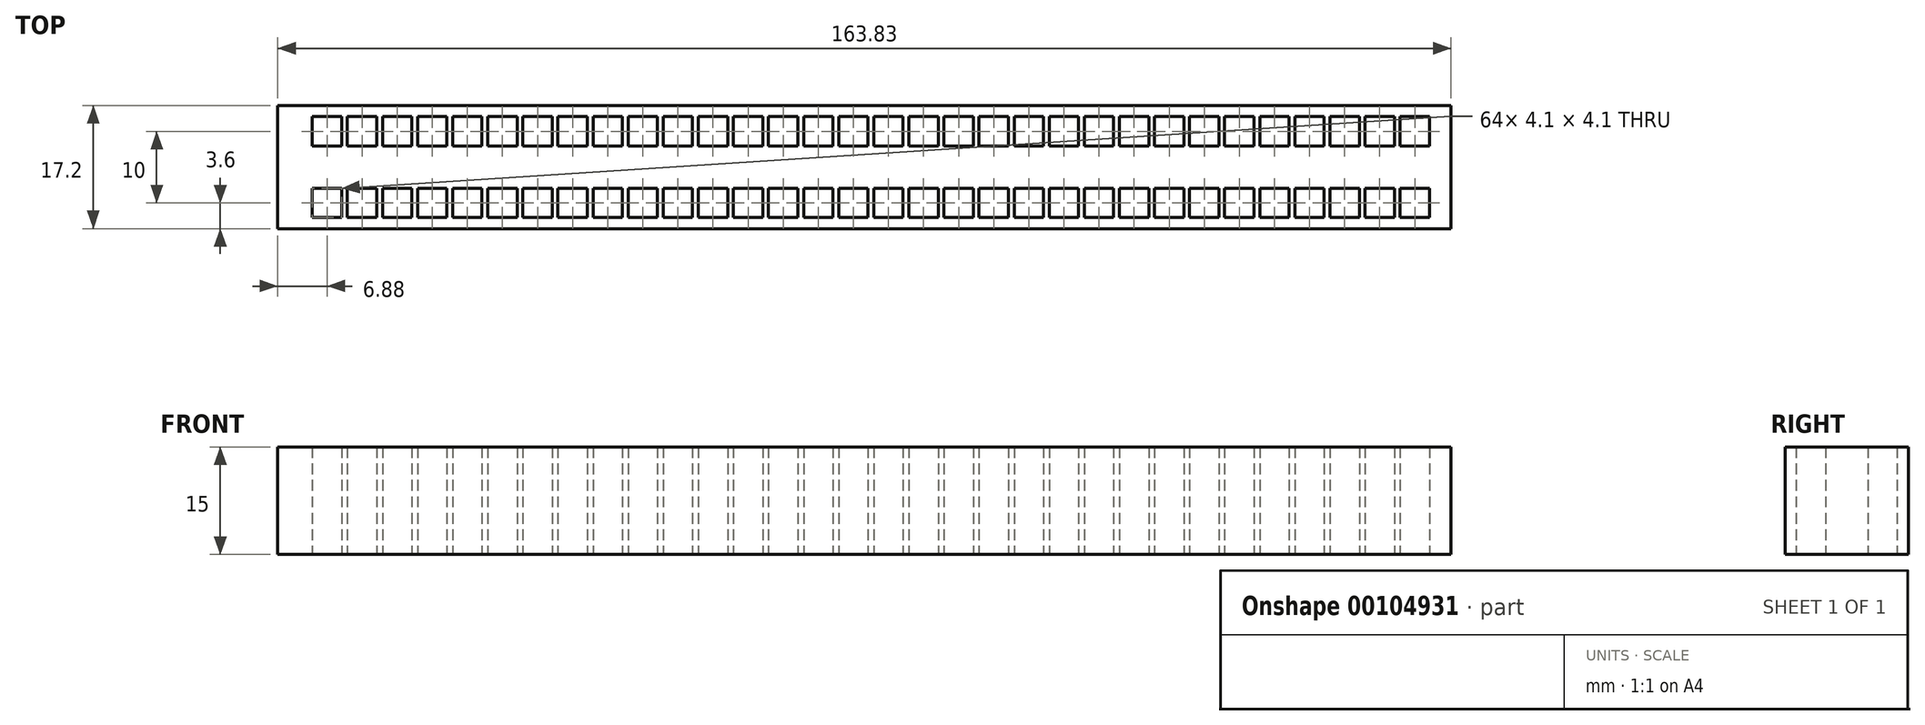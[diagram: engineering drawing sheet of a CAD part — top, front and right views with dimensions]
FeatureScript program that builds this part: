
annotation { "Feature Type Name" : "Feature", "Feature Type Description" : "" }
export const myFeature = defineFeature(function(context is Context, id is Id, definition is map)
    precondition{}
    {
        {
            var Q0;
            Q0=qCreatedBy(makeId("Top.planeOp"),FACE);
            var sketch = newSketch(context, id + "F0", { "sketchPlane" : qUnion([Q0])});
            skLineSegment(sketch, "E0", {"start": v(0, 0) * mm, "end": v(-105.59, 0) * mm});
            skLineSegment(sketch, "E1", {"start": v(0, 5) * mm, "end": v(-102.01, 5) * mm});
            skLineSegment(sketch, "E2", {"start": v(0, -8) * mm, "end": v(-106.05, -8) * mm});
            skLineSegment(sketch, "E3.bottom", {"start": v(-4.5, 7.05) * mm, "end": v(-0.4, 7.05) * mm});
            skLineSegment(sketch, "E3.top", {"start": v(-4.5, 2.95) * mm, "end": v(-0.4, 2.95) * mm});
            skLineSegment(sketch, "E3.left", {"start": v(-4.5, 7.05) * mm, "end": v(-4.5, 2.95) * mm});
            skLineSegment(sketch, "E3.right", {"start": v(-0.4, 7.05) * mm, "end": v(-0.4, 2.95) * mm});
            skPoint(sketch, "E3.middle", {"position": v(-2.45, 5) * mm});
            skLineSegment(sketch, "E4", {"start": v(0, 0) * mm, "end": v(0, 8.6) * mm, "construction": true});
            skLineSegment(sketch, "E5", {"start": v(-4.9, 0) * mm, "end": v(-4.9, 10.23) * mm, "construction": true});
            skLineSegment(sketch, "E6.MirrorCS", {"start": v(-5.3, 2.95) * mm, "end": v(-9.4, 2.95) * mm});
            skLineSegment(sketch, "E7.MirrorCS", {"start": v(-5.3, 7.05) * mm, "end": v(-5.3, 2.95) * mm});
            skLineSegment(sketch, "E8.MirrorCS", {"start": v(-5.3, 7.05) * mm, "end": v(-9.4, 7.05) * mm});
            skPoint(sketch, "E9.MirrorP", {"position": v(-7.35, 5) * mm});
            skLineSegment(sketch, "E10.MirrorCS", {"start": v(-9.4, 7.05) * mm, "end": v(-9.4, 2.95) * mm});
            skLineSegment(sketch, "E11.MirrorCS", {"start": v(-9.8, 0) * mm, "end": v(-9.8, 8.6) * mm, "construction": true});
            skLineSegment(sketch, "E12.MirrorCS", {"start": v(-9.8, 5) * mm, "end": v(92.21, 5) * mm});
            skLineSegment(sketch, "E13.MirrorCS", {"start": v(-19.6, 5) * mm, "end": v(82.41, 5) * mm, "construction": true});
            skLineSegment(sketch, "E14.MirrorCS", {"start": v(-15.1, 7.05) * mm, "end": v(-15.1, 2.95) * mm});
            skLineSegment(sketch, "E15.MirrorCS", {"start": v(-14.7, 0) * mm, "end": v(-14.7, 10.23) * mm, "construction": true});
            skLineSegment(sketch, "E16.MirrorCS", {"start": v(-19.2, 7.05) * mm, "end": v(-19.2, 2.95) * mm});
            skLineSegment(sketch, "E17.MirrorCS", {"start": v(-15.1, 2.95) * mm, "end": v(-19.2, 2.95) * mm});
            skLineSegment(sketch, "E18.MirrorCS", {"start": v(-15.1, 7.05) * mm, "end": v(-19.2, 7.05) * mm});
            skPoint(sketch, "E19.MirrorP", {"position": v(-17.15, 5) * mm});
            skPoint(sketch, "E20.MirrorP", {"position": v(-12.25, 5) * mm});
            skLineSegment(sketch, "E21.MirrorCS", {"start": v(-19.6, 0) * mm, "end": v(-19.6, 8.6) * mm, "construction": true});
            skLineSegment(sketch, "E22.MirrorCS", {"start": v(-14.3, 2.95) * mm, "end": v(-10.2, 2.95) * mm});
            skLineSegment(sketch, "E23.MirrorCS", {"start": v(-14.3, 7.05) * mm, "end": v(-14.3, 2.95) * mm});
            skLineSegment(sketch, "E24.MirrorCS", {"start": v(-14.3, 7.05) * mm, "end": v(-10.2, 7.05) * mm});
            skLineSegment(sketch, "E25.MirrorCS", {"start": v(-10.2, 7.05) * mm, "end": v(-10.2, 2.95) * mm});
            skLineSegment(sketch, "E26.MirrorCS", {"start": v(-9.8, 5) * mm, "end": v(-111.81, 5) * mm});
            skLineSegment(sketch, "E27.MirrorCS", {"start": v(-29.4, 5) * mm, "end": v(-131.41, 5) * mm});
            skLineSegment(sketch, "E28.MirrorCS", {"start": v(-29.4, 5) * mm, "end": v(72.61, 5) * mm});
            skLineSegment(sketch, "E29.MirrorCS", {"start": v(-24.5, 0) * mm, "end": v(-24.5, 10.23) * mm, "construction": true});
            skLineSegment(sketch, "E30.MirrorCS", {"start": v(-29.4, 0) * mm, "end": v(-29.4, 8.6) * mm, "construction": true});
            skLineSegment(sketch, "E31.MirrorCS", {"start": v(-24.9, 7.05) * mm, "end": v(-29, 7.05) * mm});
            skLineSegment(sketch, "E32.MirrorCS", {"start": v(-34.7, 7.05) * mm, "end": v(-38.8, 7.05) * mm});
            skLineSegment(sketch, "E33.MirrorCS", {"start": v(-19.6, 5) * mm, "end": v(-121.61, 5) * mm});
            skPoint(sketch, "E34.MirrorP", {"position": v(-22.05, 5) * mm});
            skPoint(sketch, "E35.MirrorP", {"position": v(-36.75, 5) * mm});
            skLineSegment(sketch, "E36.MirrorCS", {"start": v(-39.2, 5) * mm, "end": v(62.81, 5) * mm});
            skLineSegment(sketch, "E37.MirrorCS", {"start": v(-24.1, 2.95) * mm, "end": v(-20, 2.95) * mm});
            skLineSegment(sketch, "E38.MirrorCS", {"start": v(-34.7, 2.95) * mm, "end": v(-38.8, 2.95) * mm});
            skLineSegment(sketch, "E39.MirrorCS", {"start": v(-34.7, 7.05) * mm, "end": v(-34.7, 2.95) * mm});
            skLineSegment(sketch, "E40.MirrorCS", {"start": v(-38.8, 7.05) * mm, "end": v(-38.8, 2.95) * mm});
            skLineSegment(sketch, "E41.MirrorCS", {"start": v(-39.2, 0) * mm, "end": v(-39.2, 8.6) * mm, "construction": true});
            skLineSegment(sketch, "E42.MirrorCS", {"start": v(-34.3, 0) * mm, "end": v(-34.3, 10.23) * mm, "construction": true});
            skLineSegment(sketch, "E43.MirrorCS", {"start": v(-33.9, 2.95) * mm, "end": v(-29.8, 2.95) * mm});
            skLineSegment(sketch, "E44.MirrorCS", {"start": v(-33.9, 7.05) * mm, "end": v(-33.9, 2.95) * mm});
            skLineSegment(sketch, "E45.MirrorCS", {"start": v(-33.9, 7.05) * mm, "end": v(-29.8, 7.05) * mm});
            skLineSegment(sketch, "E46.MirrorCS", {"start": v(-29.8, 7.05) * mm, "end": v(-29.8, 2.95) * mm});
            skLineSegment(sketch, "E47.MirrorCS", {"start": v(-29, 7.05) * mm, "end": v(-29, 2.95) * mm});
            skLineSegment(sketch, "E48.MirrorCS", {"start": v(-24.9, 7.05) * mm, "end": v(-24.9, 2.95) * mm});
            skLineSegment(sketch, "E49.MirrorCS", {"start": v(-24.9, 2.95) * mm, "end": v(-29, 2.95) * mm});
            skLineSegment(sketch, "E50.MirrorCS", {"start": v(-24.1, 7.05) * mm, "end": v(-20, 7.05) * mm});
            skLineSegment(sketch, "E51.MirrorCS", {"start": v(-20, 7.05) * mm, "end": v(-20, 2.95) * mm});
            skPoint(sketch, "E52.MirrorP", {"position": v(-26.95, 5) * mm});
            skLineSegment(sketch, "E53.MirrorCS", {"start": v(-24.1, 7.05) * mm, "end": v(-24.1, 2.95) * mm});
            skPoint(sketch, "E54.MirrorP", {"position": v(-31.85, 5) * mm});
            skLineSegment(sketch, "E55.MirrorCS", {"start": v(-68.6, 5) * mm, "end": v(33.41, 5) * mm});
            skLineSegment(sketch, "E56.MirrorCS", {"start": v(-68.6, 5) * mm, "end": v(-170.61, 5) * mm});
            skLineSegment(sketch, "E57.MirrorCS", {"start": v(-58.8, 5) * mm, "end": v(-160.81, 5) * mm});
            skLineSegment(sketch, "E58.MirrorCS", {"start": v(-49, 5) * mm, "end": v(53.01, 5) * mm});
            skLineSegment(sketch, "E59.MirrorCS", {"start": v(-78.4, 5) * mm, "end": v(23.61, 5) * mm});
            skLineSegment(sketch, "E60.MirrorCS", {"start": v(-49, 5) * mm, "end": v(-151.01, 5) * mm});
            skLineSegment(sketch, "E61.MirrorCS", {"start": v(-58.8, 5) * mm, "end": v(43.21, 5) * mm});
            skLineSegment(sketch, "E62.MirrorCS", {"start": v(-68.6, 0) * mm, "end": v(-68.6, 8.6) * mm, "construction": true});
            skLineSegment(sketch, "E63.MirrorCS", {"start": v(-63.3, 7.05) * mm, "end": v(-59.2, 7.05) * mm});
            skLineSegment(sketch, "E64.MirrorCS", {"start": v(-73.1, 7.05) * mm, "end": v(-69, 7.05) * mm});
            skPoint(sketch, "E65.MirrorP", {"position": v(-41.65, 5) * mm});
            skLineSegment(sketch, "E66.MirrorCS", {"start": v(-54.3, 2.95) * mm, "end": v(-58.4, 2.95) * mm});
            skLineSegment(sketch, "E67.MirrorCS", {"start": v(-64.1, 7.05) * mm, "end": v(-64.1, 2.95) * mm});
            skPoint(sketch, "E68.MirrorP", {"position": v(-56.35, 5) * mm});
            skLineSegment(sketch, "E69.MirrorCS", {"start": v(-44.5, 7.05) * mm, "end": v(-44.5, 2.95) * mm});
            skLineSegment(sketch, "E70.MirrorCS", {"start": v(-63.3, 2.95) * mm, "end": v(-59.2, 2.95) * mm});
            skLineSegment(sketch, "E71.MirrorCS", {"start": v(-49.4, 7.05) * mm, "end": v(-49.4, 2.95) * mm});
            skLineSegment(sketch, "E72.MirrorCS", {"start": v(-43.7, 2.95) * mm, "end": v(-39.6, 2.95) * mm});
            skLineSegment(sketch, "E73.MirrorCS", {"start": v(-69, 7.05) * mm, "end": v(-69, 2.95) * mm});
            skLineSegment(sketch, "E74.MirrorCS", {"start": v(-44.5, 7.05) * mm, "end": v(-48.6, 7.05) * mm});
            skLineSegment(sketch, "E75.MirrorCS", {"start": v(-73.1, 7.05) * mm, "end": v(-73.1, 2.95) * mm});
            skLineSegment(sketch, "E76.MirrorCS", {"start": v(-73.1, 2.95) * mm, "end": v(-69, 2.95) * mm});
            skLineSegment(sketch, "E77.MirrorCS", {"start": v(-73.5, 0) * mm, "end": v(-73.5, 10.23) * mm, "construction": true});
            skLineSegment(sketch, "E78.MirrorCS", {"start": v(-78.4, 0) * mm, "end": v(-78.4, 8.6) * mm, "construction": true});
            skLineSegment(sketch, "E79.MirrorCS", {"start": v(-78, 7.05) * mm, "end": v(-78, 2.95) * mm});
            skLineSegment(sketch, "E80.MirrorCS", {"start": v(-73.9, 7.05) * mm, "end": v(-73.9, 2.95) * mm});
            skLineSegment(sketch, "E81.MirrorCS", {"start": v(-73.9, 2.95) * mm, "end": v(-78, 2.95) * mm});
            skLineSegment(sketch, "E82.MirrorCS", {"start": v(-73.9, 7.05) * mm, "end": v(-78, 7.05) * mm});
            skPoint(sketch, "E83.MirrorP", {"position": v(-46.55, 5) * mm});
            skLineSegment(sketch, "E84.MirrorCS", {"start": v(-53.9, 0) * mm, "end": v(-53.9, 10.23) * mm, "construction": true});
            skLineSegment(sketch, "E85.MirrorCS", {"start": v(-63.3, 7.05) * mm, "end": v(-63.3, 2.95) * mm});
            skPoint(sketch, "E86.MirrorP", {"position": v(-71.05, 5) * mm});
            skLineSegment(sketch, "E87.MirrorCS", {"start": v(-54.3, 7.05) * mm, "end": v(-58.4, 7.05) * mm});
            skLineSegment(sketch, "E88.MirrorCS", {"start": v(-43.7, 7.05) * mm, "end": v(-39.6, 7.05) * mm});
            skLineSegment(sketch, "E89.MirrorCS", {"start": v(-48.6, 7.05) * mm, "end": v(-48.6, 2.95) * mm});
            skLineSegment(sketch, "E90.MirrorCS", {"start": v(-44.1, 0) * mm, "end": v(-44.1, 10.23) * mm, "construction": true});
            skLineSegment(sketch, "E91.MirrorCS", {"start": v(-64.1, 7.05) * mm, "end": v(-68.2, 7.05) * mm});
            skLineSegment(sketch, "E92.MirrorCS", {"start": v(-58.8, 0) * mm, "end": v(-58.8, 8.6) * mm, "construction": true});
            skPoint(sketch, "E93.MirrorP", {"position": v(-51.45, 5) * mm});
            skLineSegment(sketch, "E94.MirrorCS", {"start": v(-53.5, 7.05) * mm, "end": v(-53.5, 2.95) * mm});
            skLineSegment(sketch, "E95.MirrorCS", {"start": v(-43.7, 7.05) * mm, "end": v(-43.7, 2.95) * mm});
            skLineSegment(sketch, "E96.MirrorCS", {"start": v(-49, 0) * mm, "end": v(-49, 8.6) * mm, "construction": true});
            skLineSegment(sketch, "E97.MirrorCS", {"start": v(-63.7, 0) * mm, "end": v(-63.7, 10.23) * mm, "construction": true});
            skPoint(sketch, "E98.MirrorP", {"position": v(-61.25, 5) * mm});
            skLineSegment(sketch, "E99.MirrorCS", {"start": v(-58.4, 7.05) * mm, "end": v(-58.4, 2.95) * mm});
            skPoint(sketch, "E100.MirrorP", {"position": v(-75.95, 5) * mm});
            skLineSegment(sketch, "E101.MirrorCS", {"start": v(-44.5, 2.95) * mm, "end": v(-48.6, 2.95) * mm});
            skLineSegment(sketch, "E102.MirrorCS", {"start": v(-68.2, 7.05) * mm, "end": v(-68.2, 2.95) * mm});
            skLineSegment(sketch, "E103.MirrorCS", {"start": v(-64.1, 2.95) * mm, "end": v(-68.2, 2.95) * mm});
            skLineSegment(sketch, "E104.MirrorCS", {"start": v(-53.5, 2.95) * mm, "end": v(-49.4, 2.95) * mm});
            skLineSegment(sketch, "E105.MirrorCS", {"start": v(-39.6, 7.05) * mm, "end": v(-39.6, 2.95) * mm});
            skLineSegment(sketch, "E106.MirrorCS", {"start": v(-53.5, 7.05) * mm, "end": v(-49.4, 7.05) * mm});
            skLineSegment(sketch, "E107.MirrorCS", {"start": v(-59.2, 7.05) * mm, "end": v(-59.2, 2.95) * mm});
            skPoint(sketch, "E108.MirrorP", {"position": v(-66.15, 5) * mm});
            skLineSegment(sketch, "E109.MirrorCS", {"start": v(-54.3, 7.05) * mm, "end": v(-54.3, 2.95) * mm});
            skLineSegment(sketch, "E110.MirrorCS", {"start": v(-39.2, 5) * mm, "end": v(-141.21, 5) * mm});
            skLineSegment(sketch, "E111.MirrorCS", {"start": v(-98, 5) * mm, "end": v(4.01, 5) * mm});
            skLineSegment(sketch, "E112.MirrorCS", {"start": v(-88.2, 5) * mm, "end": v(-190.21, 5) * mm});
            skLineSegment(sketch, "E113.MirrorCS", {"start": v(-107.8, 5) * mm, "end": v(-209.81, 5) * mm});
            skLineSegment(sketch, "E114.MirrorCS", {"start": v(-98, 5) * mm, "end": v(-200.01, 5) * mm});
            skLineSegment(sketch, "E115.MirrorCS", {"start": v(-88.2, 5) * mm, "end": v(13.81, 5) * mm});
            skLineSegment(sketch, "E116.MirrorCS", {"start": v(-147, 5) * mm, "end": v(-44.99, 5) * mm});
            skLineSegment(sketch, "E117.MirrorCS", {"start": v(-127.8, 7.05) * mm, "end": v(-127.8, 2.95) * mm});
            skLineSegment(sketch, "E118.MirrorCS", {"start": v(-107.8, 5) * mm, "end": v(-5.79, 5) * mm});
            skLineSegment(sketch, "E119.MirrorCS", {"start": v(-113.1, 7.05) * mm, "end": v(-113.1, 2.95) * mm});
            skLineSegment(sketch, "E120.MirrorCS", {"start": v(-127.4, 5) * mm, "end": v(-25.39, 5) * mm});
            skLineSegment(sketch, "E121.MirrorCS", {"start": v(-88.6, 7.05) * mm, "end": v(-88.6, 2.95) * mm});
            skLineSegment(sketch, "E122.MirrorCS", {"start": v(-118, 7.05) * mm, "end": v(-118, 2.95) * mm});
            skLineSegment(sketch, "E123.MirrorCS", {"start": v(-146.6, 7.05) * mm, "end": v(-146.6, 2.95) * mm});
            skLineSegment(sketch, "E124.MirrorCS", {"start": v(-142.5, 7.05) * mm, "end": v(-142.5, 2.95) * mm});
            skLineSegment(sketch, "E125.MirrorCS", {"start": v(-78.8, 7.05) * mm, "end": v(-78.8, 2.95) * mm});
            skLineSegment(sketch, "E126.MirrorCS", {"start": v(-98.4, 7.05) * mm, "end": v(-98.4, 2.95) * mm});
            skLineSegment(sketch, "E127.MirrorCS", {"start": v(-122.1, 7.05) * mm, "end": v(-122.1, 2.95) * mm});
            skLineSegment(sketch, "E128.MirrorCS", {"start": v(-83.7, 7.05) * mm, "end": v(-83.7, 2.95) * mm});
            skLineSegment(sketch, "E129.MirrorCS", {"start": v(-103.3, 7.05) * mm, "end": v(-103.3, 2.95) * mm});
            skLineSegment(sketch, "E130.MirrorCS", {"start": v(-87.8, 7.05) * mm, "end": v(-87.8, 2.95) * mm});
            skLineSegment(sketch, "E131.MirrorCS", {"start": v(-82.9, 7.05) * mm, "end": v(-82.9, 2.95) * mm});
            skLineSegment(sketch, "E132.MirrorCS", {"start": v(-122.9, 7.05) * mm, "end": v(-122.9, 2.95) * mm});
            skLineSegment(sketch, "E133.MirrorCS", {"start": v(-127, 7.05) * mm, "end": v(-127, 2.95) * mm});
            skLineSegment(sketch, "E134.MirrorCS", {"start": v(-127.4, 5) * mm, "end": v(-229.41, 5) * mm});
            skLineSegment(sketch, "E135.MirrorCS", {"start": v(-93.5, 7.05) * mm, "end": v(-93.5, 2.95) * mm});
            skLineSegment(sketch, "E136.MirrorCS", {"start": v(-92.7, 7.05) * mm, "end": v(-92.7, 2.95) * mm});
            skLineSegment(sketch, "E137.MirrorCS", {"start": v(-131.9, 7.05) * mm, "end": v(-131.9, 2.95) * mm});
            skLineSegment(sketch, "E138.MirrorCS", {"start": v(-117.2, 7.05) * mm, "end": v(-117.2, 2.95) * mm});
            skLineSegment(sketch, "E139.MirrorCS", {"start": v(-112.3, 7.05) * mm, "end": v(-112.3, 2.95) * mm});
            skLineSegment(sketch, "E140.MirrorCS", {"start": v(-147, 5) * mm, "end": v(-249.01, 5) * mm});
            skLineSegment(sketch, "E141.MirrorCS", {"start": v(-137.6, 7.05) * mm, "end": v(-137.6, 2.95) * mm});
            skLineSegment(sketch, "E142.MirrorCS", {"start": v(-97.6, 7.05) * mm, "end": v(-97.6, 2.95) * mm});
            skLineSegment(sketch, "E143.MirrorCS", {"start": v(-108.2, 7.05) * mm, "end": v(-108.2, 2.95) * mm});
            skLineSegment(sketch, "E144.MirrorCS", {"start": v(-136.8, 7.05) * mm, "end": v(-136.8, 2.95) * mm});
            skLineSegment(sketch, "E145.MirrorCS", {"start": v(-107.4, 7.05) * mm, "end": v(-107.4, 2.95) * mm});
            skLineSegment(sketch, "E146.MirrorCS", {"start": v(-147.4, 7.05) * mm, "end": v(-147.4, 2.95) * mm});
            skLineSegment(sketch, "E147.MirrorCS", {"start": v(-78.4, 5) * mm, "end": v(-180.41, 5) * mm});
            skLineSegment(sketch, "E148.MirrorCS", {"start": v(-137.2, 5) * mm, "end": v(-239.21, 5) * mm});
            skLineSegment(sketch, "E149.MirrorCS", {"start": v(-156.8, 5) * mm, "end": v(-54.79, 5) * mm});
            skLineSegment(sketch, "E150.MirrorCS", {"start": v(-152.3, 7.05) * mm, "end": v(-152.3, 2.95) * mm});
            skLineSegment(sketch, "E151.MirrorCS", {"start": v(-156.4, 7.05) * mm, "end": v(-156.4, 2.95) * mm});
            skLineSegment(sketch, "E152.MirrorCS", {"start": v(-151.9, 0) * mm, "end": v(-151.9, 10.23) * mm, "construction": true});
            skLineSegment(sketch, "E153.MirrorCS", {"start": v(-151.5, 7.05) * mm, "end": v(-151.5, 2.95) * mm});
            skLineSegment(sketch, "E154.MirrorCS", {"start": v(-151.5, 7.05) * mm, "end": v(-147.4, 7.05) * mm});
            skLineSegment(sketch, "E155.MirrorCS", {"start": v(-137.2, 5) * mm, "end": v(-35.19, 5) * mm});
            skLineSegment(sketch, "E156.MirrorCS", {"start": v(-102.5, 7.05) * mm, "end": v(-102.5, 2.95) * mm});
            skLineSegment(sketch, "E157.MirrorCS", {"start": v(-132.7, 7.05) * mm, "end": v(-132.7, 2.95) * mm});
            skLineSegment(sketch, "E158.MirrorCS", {"start": v(-141.7, 7.05) * mm, "end": v(-141.7, 2.95) * mm});
            skLineSegment(sketch, "E159.MirrorCS", {"start": v(-132.3, 0) * mm, "end": v(-132.3, 10.23) * mm, "construction": true});
            skPoint(sketch, "E160.MirrorP", {"position": v(-124.95, 5) * mm});
            skLineSegment(sketch, "E161.MirrorCS", {"start": v(-93.1, 0) * mm, "end": v(-93.1, 10.23) * mm, "construction": true});
            skLineSegment(sketch, "E162.MirrorCS", {"start": v(-122.5, 0) * mm, "end": v(-122.5, 10.23) * mm, "construction": true});
            skLineSegment(sketch, "E163.MirrorCS", {"start": v(-142.5, 7.05) * mm, "end": v(-146.6, 7.05) * mm});
            skLineSegment(sketch, "E164.MirrorCS", {"start": v(-83.7, 2.95) * mm, "end": v(-87.8, 2.95) * mm});
            skPoint(sketch, "E165.MirrorP", {"position": v(-154.35, 5) * mm});
            skLineSegment(sketch, "E166.MirrorCS", {"start": v(-142.5, 2.95) * mm, "end": v(-146.6, 2.95) * mm});
            skPoint(sketch, "E167.MirrorP", {"position": v(-139.65, 5) * mm});
            skLineSegment(sketch, "E168.MirrorCS", {"start": v(-122.9, 7.05) * mm, "end": v(-127, 7.05) * mm});
            skLineSegment(sketch, "E169.MirrorCS", {"start": v(-93.5, 7.05) * mm, "end": v(-97.6, 7.05) * mm});
            skLineSegment(sketch, "E170.MirrorCS", {"start": v(-82.9, 2.95) * mm, "end": v(-78.8, 2.95) * mm});
            skLineSegment(sketch, "E171.MirrorCS", {"start": v(-122.9, 2.95) * mm, "end": v(-127, 2.95) * mm});
            skPoint(sketch, "E172.MirrorP", {"position": v(-149.45, 5) * mm});
            skLineSegment(sketch, "E173.MirrorCS", {"start": v(-117.6, 0) * mm, "end": v(-117.6, 8.6) * mm, "construction": true});
            skLineSegment(sketch, "E174.MirrorCS", {"start": v(-107.8, 0) * mm, "end": v(-107.8, 8.6) * mm, "construction": true});
            skLineSegment(sketch, "E175.MirrorCS", {"start": v(-83.3, 0) * mm, "end": v(-83.3, 10.23) * mm, "construction": true});
            skLineSegment(sketch, "E176.MirrorCS", {"start": v(-102.5, 2.95) * mm, "end": v(-98.4, 2.95) * mm});
            skLineSegment(sketch, "E177.MirrorCS", {"start": v(-102.9, 0) * mm, "end": v(-102.9, 10.23) * mm, "construction": true});
            skLineSegment(sketch, "E178.MirrorCS", {"start": v(-103.3, 2.95) * mm, "end": v(-107.4, 2.95) * mm});
            skPoint(sketch, "E179.MirrorP", {"position": v(-120.05, 5) * mm});
            skLineSegment(sketch, "E180.MirrorCS", {"start": v(-137.2, 0) * mm, "end": v(-137.2, 8.6) * mm, "construction": true});
            skPoint(sketch, "E181.MirrorP", {"position": v(-90.65, 5) * mm});
            skLineSegment(sketch, "E182.MirrorCS", {"start": v(-122.1, 2.95) * mm, "end": v(-118, 2.95) * mm});
            skLineSegment(sketch, "E183.MirrorCS", {"start": v(-112.3, 7.05) * mm, "end": v(-108.2, 7.05) * mm});
            skLineSegment(sketch, "E184.MirrorCS", {"start": v(-98, 0) * mm, "end": v(-98, 8.6) * mm, "construction": true});
            skLineSegment(sketch, "E185.MirrorCS", {"start": v(-141.7, 7.05) * mm, "end": v(-137.6, 7.05) * mm});
            skPoint(sketch, "E186.MirrorP", {"position": v(-80.85, 5) * mm});
            skPoint(sketch, "E187.MirrorP", {"position": v(-134.75, 5) * mm});
            skLineSegment(sketch, "E188.MirrorCS", {"start": v(-132.7, 2.95) * mm, "end": v(-136.8, 2.95) * mm});
            skLineSegment(sketch, "E189.MirrorCS", {"start": v(-92.7, 7.05) * mm, "end": v(-88.6, 7.05) * mm});
            skLineSegment(sketch, "E190.MirrorCS", {"start": v(-141.7, 2.95) * mm, "end": v(-137.6, 2.95) * mm});
            skPoint(sketch, "E191.MirrorP", {"position": v(-95.55, 5) * mm});
            skLineSegment(sketch, "E192.MirrorCS", {"start": v(-112.3, 2.95) * mm, "end": v(-108.2, 2.95) * mm});
            skLineSegment(sketch, "E193.MirrorCS", {"start": v(-88.2, 0) * mm, "end": v(-88.2, 8.6) * mm, "construction": true});
            skPoint(sketch, "E194.MirrorP", {"position": v(-144.55, 5) * mm});
            skPoint(sketch, "E195.MirrorP", {"position": v(-115.15, 5) * mm});
            skLineSegment(sketch, "E196.MirrorCS", {"start": v(-83.7, 7.05) * mm, "end": v(-87.8, 7.05) * mm});
            skLineSegment(sketch, "E197.MirrorCS", {"start": v(-92.7, 2.95) * mm, "end": v(-88.6, 2.95) * mm});
            skLineSegment(sketch, "E198.MirrorCS", {"start": v(-82.9, 7.05) * mm, "end": v(-78.8, 7.05) * mm});
            skLineSegment(sketch, "E199.MirrorCS", {"start": v(-127.4, 0) * mm, "end": v(-127.4, 8.6) * mm, "construction": true});
            skPoint(sketch, "E200.MirrorP", {"position": v(-129.85, 5) * mm});
            skPoint(sketch, "E201.MirrorP", {"position": v(-100.45, 5) * mm});
            skLineSegment(sketch, "E202.MirrorCS", {"start": v(-102.5, 7.05) * mm, "end": v(-98.4, 7.05) * mm});
            skLineSegment(sketch, "E203.MirrorCS", {"start": v(-131.9, 2.95) * mm, "end": v(-127.8, 2.95) * mm});
            skLineSegment(sketch, "E204.MirrorCS", {"start": v(-131.9, 7.05) * mm, "end": v(-127.8, 7.05) * mm});
            skLineSegment(sketch, "E205.MirrorCS", {"start": v(-103.3, 7.05) * mm, "end": v(-107.4, 7.05) * mm});
            skLineSegment(sketch, "E206.MirrorCS", {"start": v(-147, 0) * mm, "end": v(-147, 8.6) * mm, "construction": true});
            skLineSegment(sketch, "E207.MirrorCS", {"start": v(-152.3, 7.05) * mm, "end": v(-156.4, 7.05) * mm});
            skLineSegment(sketch, "E208.MirrorCS", {"start": v(-152.3, 2.95) * mm, "end": v(-156.4, 2.95) * mm});
            skLineSegment(sketch, "E209.MirrorCS", {"start": v(-156.8, 0) * mm, "end": v(-156.8, 8.6) * mm, "construction": true});
            skLineSegment(sketch, "E210.MirrorCS", {"start": v(-151.5, 2.95) * mm, "end": v(-147.4, 2.95) * mm});
            skLineSegment(sketch, "E211.MirrorCS", {"start": v(-93.5, 2.95) * mm, "end": v(-97.6, 2.95) * mm});
            skLineSegment(sketch, "E212.MirrorCS", {"start": v(-122.1, 7.05) * mm, "end": v(-118, 7.05) * mm});
            skPoint(sketch, "E213.MirrorP", {"position": v(-85.75, 5) * mm});
            skLineSegment(sketch, "E214.MirrorCS", {"start": v(-142.1, 0) * mm, "end": v(-142.1, 10.23) * mm, "construction": true});
            skPoint(sketch, "E215.MirrorP", {"position": v(-105.35, 5) * mm});
            skLineSegment(sketch, "E216.MirrorCS", {"start": v(-112.7, 0) * mm, "end": v(-112.7, 10.23) * mm, "construction": true});
            skLineSegment(sketch, "E217.MirrorCS", {"start": v(-113.1, 2.95) * mm, "end": v(-117.2, 2.95) * mm});
            skLineSegment(sketch, "E218.MirrorCS", {"start": v(-117.6, 5) * mm, "end": v(-219.61, 5) * mm});
            skLineSegment(sketch, "E219.MirrorCS", {"start": v(-117.6, 5) * mm, "end": v(-15.59, 5) * mm});
            skPoint(sketch, "E220.MirrorP", {"position": v(-110.25, 5) * mm});
            skLineSegment(sketch, "E221.MirrorCS", {"start": v(-113.1, 7.05) * mm, "end": v(-117.2, 7.05) * mm});
            skLineSegment(sketch, "E222.MirrorCS", {"start": v(-132.7, 7.05) * mm, "end": v(-136.8, 7.05) * mm});
            skLineSegment(sketch, "E223.MirrorCS", {"start": v(-14.3, -7.05) * mm, "end": v(-14.3, -2.95) * mm});
            skLineSegment(sketch, "E224.MirrorCS", {"start": v(-82.9, -7.05) * mm, "end": v(-82.9, -2.95) * mm});
            skLineSegment(sketch, "E225.MirrorCS", {"start": v(-102.5, -7.05) * mm, "end": v(-102.5, -2.95) * mm});
            skLineSegment(sketch, "E226.MirrorCS", {"start": v(-9.4, -7.05) * mm, "end": v(-9.4, -2.95) * mm});
            skLineSegment(sketch, "E227.MirrorCS", {"start": v(-59.2, -7.05) * mm, "end": v(-59.2, -2.95) * mm});
            skLineSegment(sketch, "E228.MirrorCS", {"start": v(-4.5, -7.05) * mm, "end": v(-4.5, -2.95) * mm});
            skLineSegment(sketch, "E229.MirrorCS", {"start": v(-78, -7.05) * mm, "end": v(-78, -2.95) * mm});
            skLineSegment(sketch, "E230.MirrorCS", {"start": v(-58.4, -7.05) * mm, "end": v(-58.4, -2.95) * mm});
            skLineSegment(sketch, "E231.MirrorCS", {"start": v(-127.8, -7.05) * mm, "end": v(-127.8, -2.95) * mm});
            skLineSegment(sketch, "E232.MirrorCS", {"start": v(-10.2, -7.05) * mm, "end": v(-10.2, -2.95) * mm});
            skLineSegment(sketch, "E233.MirrorCS", {"start": v(-127, -7.05) * mm, "end": v(-127, -2.95) * mm});
            skLineSegment(sketch, "E234.MirrorCS", {"start": v(-5.3, -7.05) * mm, "end": v(-5.3, -2.95) * mm});
            skLineSegment(sketch, "E235.MirrorCS", {"start": v(-122.9, -7.05) * mm, "end": v(-122.9, -2.95) * mm});
            skLineSegment(sketch, "E236.MirrorCS", {"start": v(-87.8, -7.05) * mm, "end": v(-87.8, -2.95) * mm});
            skLineSegment(sketch, "E237.MirrorCS", {"start": v(-147.4, -7.05) * mm, "end": v(-147.4, -2.95) * mm});
            skLineSegment(sketch, "E238.MirrorCS", {"start": v(-38.8, -7.05) * mm, "end": v(-38.8, -2.95) * mm});
            skLineSegment(sketch, "E239.MirrorCS", {"start": v(-48.6, -7.05) * mm, "end": v(-48.6, -2.95) * mm});
            skLineSegment(sketch, "E240.MirrorCS", {"start": v(-49.4, -7.05) * mm, "end": v(-49.4, -2.95) * mm});
            skLineSegment(sketch, "E241.MirrorCS", {"start": v(-20, -7.05) * mm, "end": v(-20, -2.95) * mm});
            skLineSegment(sketch, "E242.MirrorCS", {"start": v(-137.6, -7.05) * mm, "end": v(-137.6, -2.95) * mm});
            skLineSegment(sketch, "E243.MirrorCS", {"start": v(-132.7, -7.05) * mm, "end": v(-132.7, -2.95) * mm});
            skLineSegment(sketch, "E244.MirrorCS", {"start": v(-54.3, -7.05) * mm, "end": v(-54.3, -2.95) * mm});
            skLineSegment(sketch, "E245.MirrorCS", {"start": v(-78.8, -7.05) * mm, "end": v(-78.8, -2.95) * mm});
            skLineSegment(sketch, "E246.MirrorCS", {"start": v(-33.9, -7.05) * mm, "end": v(-33.9, -2.95) * mm});
            skLineSegment(sketch, "E247.MirrorCS", {"start": v(-107.8, -5) * mm, "end": v(-5.79, -5) * mm});
            skLineSegment(sketch, "E248.MirrorCS", {"start": v(-73.9, -7.05) * mm, "end": v(-73.9, -2.95) * mm});
            skLineSegment(sketch, "E249.MirrorCS", {"start": v(-19.2, -7.05) * mm, "end": v(-19.2, -2.95) * mm});
            skLineSegment(sketch, "E250.MirrorCS", {"start": v(-97.6, -7.05) * mm, "end": v(-97.6, -2.95) * mm});
            skLineSegment(sketch, "E251.MirrorCS", {"start": v(-98.4, -7.05) * mm, "end": v(-98.4, -2.95) * mm});
            skLineSegment(sketch, "E252.MirrorCS", {"start": v(-43.7, -7.05) * mm, "end": v(-43.7, -2.95) * mm});
            skLineSegment(sketch, "E253.MirrorCS", {"start": v(-146.6, -7.05) * mm, "end": v(-146.6, -2.95) * mm});
            skLineSegment(sketch, "E254.MirrorCS", {"start": v(-112.3, -7.05) * mm, "end": v(-112.3, -2.95) * mm});
            skLineSegment(sketch, "E255.MirrorCS", {"start": v(-44.5, -7.05) * mm, "end": v(-44.5, -2.95) * mm});
            skLineSegment(sketch, "E256.MirrorCS", {"start": v(-103.3, -7.05) * mm, "end": v(-103.3, -2.95) * mm});
            skLineSegment(sketch, "E257.MirrorCS", {"start": v(-107.4, -7.05) * mm, "end": v(-107.4, -2.95) * mm});
            skLineSegment(sketch, "E258.MirrorCS", {"start": v(-34.7, -7.05) * mm, "end": v(-34.7, -2.95) * mm});
            skLineSegment(sketch, "E259.MirrorCS", {"start": v(-73.1, -7.05) * mm, "end": v(-73.1, -2.95) * mm});
            skLineSegment(sketch, "E260.MirrorCS", {"start": v(-53.5, -7.05) * mm, "end": v(-53.5, -2.95) * mm});
            skLineSegment(sketch, "E261.MirrorCS", {"start": v(-39.6, -7.05) * mm, "end": v(-39.6, -2.95) * mm});
            skLineSegment(sketch, "E262.MirrorCS", {"start": v(-83.7, -7.05) * mm, "end": v(-83.7, -2.95) * mm});
            skLineSegment(sketch, "E263.MirrorCS", {"start": v(-136.8, -7.05) * mm, "end": v(-136.8, -2.95) * mm});
            skLineSegment(sketch, "E264.MirrorCS", {"start": v(-118, -7.05) * mm, "end": v(-118, -2.95) * mm});
            skLineSegment(sketch, "E265.MirrorCS", {"start": v(-117.2, -7.05) * mm, "end": v(-117.2, -2.95) * mm});
            skLineSegment(sketch, "E266.MirrorCS", {"start": v(-24.9, -7.05) * mm, "end": v(-24.9, -2.95) * mm});
            skLineSegment(sketch, "E267.MirrorCS", {"start": v(-64.1, -7.05) * mm, "end": v(-64.1, -2.95) * mm});
            skLineSegment(sketch, "E268.MirrorCS", {"start": v(-63.3, -7.05) * mm, "end": v(-63.3, -2.95) * mm});
            skLineSegment(sketch, "E269.MirrorCS", {"start": v(-92.7, -7.05) * mm, "end": v(-92.7, -2.95) * mm});
            skLineSegment(sketch, "E270.MirrorCS", {"start": v(-29.8, -7.05) * mm, "end": v(-29.8, -2.95) * mm});
            skLineSegment(sketch, "E271.MirrorCS", {"start": v(-88.6, -7.05) * mm, "end": v(-88.6, -2.95) * mm});
            skLineSegment(sketch, "E272.MirrorCS", {"start": v(-131.9, -7.05) * mm, "end": v(-131.9, -2.95) * mm});
            skLineSegment(sketch, "E273.MirrorCS", {"start": v(-29, -7.05) * mm, "end": v(-29, -2.95) * mm});
            skLineSegment(sketch, "E274.MirrorCS", {"start": v(-108.2, -7.05) * mm, "end": v(-108.2, -2.95) * mm});
            skLineSegment(sketch, "E275.MirrorCS", {"start": v(-68.2, -7.05) * mm, "end": v(-68.2, -2.95) * mm});
            skLineSegment(sketch, "E276.MirrorCS", {"start": v(-93.5, -7.05) * mm, "end": v(-93.5, -2.95) * mm});
            skLineSegment(sketch, "E277.MirrorCS", {"start": v(-113.1, -7.05) * mm, "end": v(-113.1, -2.95) * mm});
            skLineSegment(sketch, "E278.MirrorCS", {"start": v(-122.1, -7.05) * mm, "end": v(-122.1, -2.95) * mm});
            skLineSegment(sketch, "E279.MirrorCS", {"start": v(-69, -7.05) * mm, "end": v(-69, -2.95) * mm});
            skLineSegment(sketch, "E280.MirrorCS", {"start": v(-0.4, -7.05) * mm, "end": v(-0.4, -2.95) * mm});
            skLineSegment(sketch, "E281.MirrorCS", {"start": v(-142.5, -7.05) * mm, "end": v(-142.5, -2.95) * mm});
            skLineSegment(sketch, "E282.MirrorCS", {"start": v(-63.3, -2.95) * mm, "end": v(-59.2, -2.95) * mm});
            skLineSegment(sketch, "E283.MirrorCS", {"start": v(-4.9, 0) * mm, "end": v(-4.9, -10.23) * mm, "construction": true});
            skLineSegment(sketch, "E284.MirrorCS", {"start": v(-117.6, -5) * mm, "end": v(-15.59, -5) * mm});
            skLineSegment(sketch, "E285.MirrorCS", {"start": v(-15.1, -7.05) * mm, "end": v(-15.1, -2.95) * mm});
            skLineSegment(sketch, "E286.MirrorCS", {"start": v(-5.3, -7.05) * mm, "end": v(-9.4, -7.05) * mm});
            skLineSegment(sketch, "E287.MirrorCS", {"start": v(-142.5, -2.95) * mm, "end": v(-146.6, -2.95) * mm});
            skLineSegment(sketch, "E288.MirrorCS", {"start": v(-156.8, -5) * mm, "end": v(-54.79, -5) * mm});
            skLineSegment(sketch, "E289.MirrorCS", {"start": v(-132.7, -2.95) * mm, "end": v(-136.8, -2.95) * mm});
            skLineSegment(sketch, "E290.MirrorCS", {"start": v(-4.5, -2.95) * mm, "end": v(-0.4, -2.95) * mm});
            skLineSegment(sketch, "E291.MirrorCS", {"start": v(-151.5, -2.95) * mm, "end": v(-147.4, -2.95) * mm});
            skLineSegment(sketch, "E292.MirrorCS", {"start": v(-147, -5) * mm, "end": v(-44.99, -5) * mm});
            skLineSegment(sketch, "E293.MirrorCS", {"start": v(-33.9, -2.95) * mm, "end": v(-29.8, -2.95) * mm});
            skLineSegment(sketch, "E294.MirrorCS", {"start": v(-5.3, -2.95) * mm, "end": v(-9.4, -2.95) * mm});
            skLineSegment(sketch, "E295.MirrorCS", {"start": v(-73.1, -2.95) * mm, "end": v(-69, -2.95) * mm});
            skLineSegment(sketch, "E296.MirrorCS", {"start": v(-49, -5) * mm, "end": v(-151.01, -5) * mm});
            skLineSegment(sketch, "E297.MirrorCS", {"start": v(-102.5, -2.95) * mm, "end": v(-98.4, -2.95) * mm});
            skLineSegment(sketch, "E298.MirrorCS", {"start": v(-19.6, -5) * mm, "end": v(-121.61, -5) * mm});
            skLineSegment(sketch, "E299.MirrorCS", {"start": v(-9.8, -5) * mm, "end": v(-111.81, -5) * mm});
            skLineSegment(sketch, "E300.MirrorCS", {"start": v(-44.5, -2.95) * mm, "end": v(-48.6, -2.95) * mm});
            skLineSegment(sketch, "E301.MirrorCS", {"start": v(-93.5, -2.95) * mm, "end": v(-97.6, -2.95) * mm});
            skLineSegment(sketch, "E302.MirrorCS", {"start": v(-141.7, -2.95) * mm, "end": v(-137.6, -2.95) * mm});
            skLineSegment(sketch, "E303.MirrorCS", {"start": v(-152.3, -7.05) * mm, "end": v(-152.3, -2.95) * mm});
            skLineSegment(sketch, "E304.MirrorCS", {"start": v(-152.3, -2.95) * mm, "end": v(-156.4, -2.95) * mm});
            skLineSegment(sketch, "E305.MirrorCS", {"start": v(-83.7, -2.95) * mm, "end": v(-87.8, -2.95) * mm});
            skLineSegment(sketch, "E306.MirrorCS", {"start": v(-43.7, -2.95) * mm, "end": v(-39.6, -2.95) * mm});
            skLineSegment(sketch, "E307.MirrorCS", {"start": v(-24.1, -7.05) * mm, "end": v(-24.1, -2.95) * mm});
            skLineSegment(sketch, "E308.MirrorCS", {"start": v(-141.7, -7.05) * mm, "end": v(-141.7, -2.95) * mm});
            skLineSegment(sketch, "E309.MirrorCS", {"start": v(-39.2, -5) * mm, "end": v(-141.21, -5) * mm});
            skLineSegment(sketch, "E310.MirrorCS", {"start": v(-131.9, -2.95) * mm, "end": v(-127.8, -2.95) * mm});
            skLineSegment(sketch, "E311.MirrorCS", {"start": v(-103.3, -2.95) * mm, "end": v(-107.4, -2.95) * mm});
            skLineSegment(sketch, "E312.MirrorCS", {"start": v(0, -5) * mm, "end": v(-102.01, -5) * mm});
            skLineSegment(sketch, "E313.MirrorCS", {"start": v(-14.3, -2.95) * mm, "end": v(-10.2, -2.95) * mm});
            skLineSegment(sketch, "E314.MirrorCS", {"start": v(-137.2, -5) * mm, "end": v(-35.19, -5) * mm});
            skLineSegment(sketch, "E315.MirrorCS", {"start": v(-24.9, -2.95) * mm, "end": v(-29, -2.95) * mm});
            skLineSegment(sketch, "E316.MirrorCS", {"start": v(-92.7, -2.95) * mm, "end": v(-88.6, -2.95) * mm});
            skLineSegment(sketch, "E317.MirrorCS", {"start": v(-113.1, -2.95) * mm, "end": v(-117.2, -2.95) * mm});
            skLineSegment(sketch, "E318.MirrorCS", {"start": v(-122.1, -2.95) * mm, "end": v(-118, -2.95) * mm});
            skLineSegment(sketch, "E319.MirrorCS", {"start": v(-34.7, -2.95) * mm, "end": v(-38.8, -2.95) * mm});
            skLineSegment(sketch, "E320.MirrorCS", {"start": v(-122.9, -2.95) * mm, "end": v(-127, -2.95) * mm});
            skLineSegment(sketch, "E321.MirrorCS", {"start": v(-64.1, -2.95) * mm, "end": v(-68.2, -2.95) * mm});
            skLineSegment(sketch, "E322.MirrorCS", {"start": v(-127.4, -5) * mm, "end": v(-25.39, -5) * mm});
            skLineSegment(sketch, "E323.MirrorCS", {"start": v(-151.5, -7.05) * mm, "end": v(-151.5, -2.95) * mm});
            skLineSegment(sketch, "E324.MirrorCS", {"start": v(-54.3, -2.95) * mm, "end": v(-58.4, -2.95) * mm});
            skLineSegment(sketch, "E325.MirrorCS", {"start": v(-15.1, -2.95) * mm, "end": v(-19.2, -2.95) * mm});
            skLineSegment(sketch, "E326.MirrorCS", {"start": v(-73.9, -2.95) * mm, "end": v(-78, -2.95) * mm});
            skLineSegment(sketch, "E327.MirrorCS", {"start": v(-29.4, -5) * mm, "end": v(-131.41, -5) * mm});
            skLineSegment(sketch, "E328.MirrorCS", {"start": v(-82.9, -2.95) * mm, "end": v(-78.8, -2.95) * mm});
            skLineSegment(sketch, "E329.MirrorCS", {"start": v(-53.5, -2.95) * mm, "end": v(-49.4, -2.95) * mm});
            skLineSegment(sketch, "E330.MirrorCS", {"start": v(-24.1, -2.95) * mm, "end": v(-20, -2.95) * mm});
            skLineSegment(sketch, "E331.MirrorCS", {"start": v(-156.4, -7.05) * mm, "end": v(-156.4, -2.95) * mm});
            skLineSegment(sketch, "E332.MirrorCS", {"start": v(-112.3, -2.95) * mm, "end": v(-108.2, -2.95) * mm});
            skPoint(sketch, "E333.MirrorP", {"position": v(-149.45, -5) * mm});
            skLineSegment(sketch, "E334.MirrorCS", {"start": v(-43.7, -7.05) * mm, "end": v(-39.6, -7.05) * mm});
            skLineSegment(sketch, "E335.MirrorCS", {"start": v(-14.7, 0) * mm, "end": v(-14.7, -10.23) * mm, "construction": true});
            skPoint(sketch, "E336.MirrorP", {"position": v(-71.05, -5) * mm});
            skPoint(sketch, "E337.MirrorP", {"position": v(-129.85, -5) * mm});
            skPoint(sketch, "E338.MirrorP", {"position": v(-12.25, -5) * mm});
            skLineSegment(sketch, "E339.MirrorCS", {"start": v(-34.7, -7.05) * mm, "end": v(-38.8, -7.05) * mm});
            skLineSegment(sketch, "E340.MirrorCS", {"start": v(-24.1, -7.05) * mm, "end": v(-20, -7.05) * mm});
            skPoint(sketch, "E341.MirrorP", {"position": v(-7.35, -5) * mm});
            skLineSegment(sketch, "E342.MirrorCS", {"start": v(0, 0) * mm, "end": v(0, -8.6) * mm, "construction": true});
            skLineSegment(sketch, "E343.MirrorCS", {"start": v(-39.2, 0) * mm, "end": v(-39.2, -8.6) * mm, "construction": true});
            skPoint(sketch, "E344.MirrorP", {"position": v(-154.35, -5) * mm});
            skPoint(sketch, "E345.MirrorP", {"position": v(-115.15, -5) * mm});
            skPoint(sketch, "E346.MirrorP", {"position": v(-46.55, -5) * mm});
            skLineSegment(sketch, "E347.MirrorCS", {"start": v(-122.9, -7.05) * mm, "end": v(-127, -7.05) * mm});
            skLineSegment(sketch, "E348.MirrorCS", {"start": v(-92.7, -7.05) * mm, "end": v(-88.6, -7.05) * mm});
            skLineSegment(sketch, "E349.MirrorCS", {"start": v(-78.4, 0) * mm, "end": v(-78.4, -8.6) * mm, "construction": true});
            skLineSegment(sketch, "E350.MirrorCS", {"start": v(-156.8, 0) * mm, "end": v(-156.8, -8.6) * mm, "construction": true});
            skLineSegment(sketch, "E351.MirrorCS", {"start": v(-63.7, 0) * mm, "end": v(-63.7, -10.23) * mm, "construction": true});
            skLineSegment(sketch, "E352.MirrorCS", {"start": v(-4.5, -7.05) * mm, "end": v(-0.4, -7.05) * mm});
            skLineSegment(sketch, "E353.MirrorCS", {"start": v(-102.5, -7.05) * mm, "end": v(-98.4, -7.05) * mm});
            skLineSegment(sketch, "E354.MirrorCS", {"start": v(-102.9, 0) * mm, "end": v(-102.9, -10.23) * mm, "construction": true});
            skLineSegment(sketch, "E355.MirrorCS", {"start": v(-14.3, -7.05) * mm, "end": v(-10.2, -7.05) * mm});
            skLineSegment(sketch, "E356.MirrorCS", {"start": v(-34.3, 0) * mm, "end": v(-34.3, -10.23) * mm, "construction": true});
            skLineSegment(sketch, "E357.MirrorCS", {"start": v(-98, 0) * mm, "end": v(-98, -8.6) * mm, "construction": true});
            skLineSegment(sketch, "E358.MirrorCS", {"start": v(-152.3, -7.05) * mm, "end": v(-156.4, -7.05) * mm});
            skLineSegment(sketch, "E359.MirrorCS", {"start": v(-113.1, -7.05) * mm, "end": v(-117.2, -7.05) * mm});
            skLineSegment(sketch, "E360.MirrorCS", {"start": v(-142.5, -7.05) * mm, "end": v(-146.6, -7.05) * mm});
            skLineSegment(sketch, "E361.MirrorCS", {"start": v(-127.4, 0) * mm, "end": v(-127.4, -8.6) * mm, "construction": true});
            skPoint(sketch, "E362.MirrorP", {"position": v(-120.05, -5) * mm});
            skPoint(sketch, "E363.MirrorP", {"position": v(-22.05, -5) * mm});
            skLineSegment(sketch, "E364.MirrorCS", {"start": v(-68.6, 0) * mm, "end": v(-68.6, -8.6) * mm, "construction": true});
            skLineSegment(sketch, "E365.MirrorCS", {"start": v(-93.5, -7.05) * mm, "end": v(-97.6, -7.05) * mm});
            skLineSegment(sketch, "E366.MirrorCS", {"start": v(-49, 0) * mm, "end": v(-49, -8.6) * mm, "construction": true});
            skLineSegment(sketch, "E367.MirrorCS", {"start": v(-73.5, 0) * mm, "end": v(-73.5, -10.23) * mm, "construction": true});
            skPoint(sketch, "E368.MirrorP", {"position": v(-51.45, -5) * mm});
            skPoint(sketch, "E369.MirrorP", {"position": v(-100.45, -5) * mm});
            skLineSegment(sketch, "E370.MirrorCS", {"start": v(-141.7, -7.05) * mm, "end": v(-137.6, -7.05) * mm});
            skLineSegment(sketch, "E371.MirrorCS", {"start": v(-44.1, 0) * mm, "end": v(-44.1, -10.23) * mm, "construction": true});
            skLineSegment(sketch, "E372.MirrorCS", {"start": v(-132.7, -7.05) * mm, "end": v(-136.8, -7.05) * mm});
            skPoint(sketch, "E373.MirrorP", {"position": v(-139.65, -5) * mm});
            skPoint(sketch, "E374.MirrorP", {"position": v(-17.15, -5) * mm});
            skPoint(sketch, "E375.MirrorP", {"position": v(-124.95, -5) * mm});
            skPoint(sketch, "E376.MirrorP", {"position": v(-2.45, -5) * mm});
            skLineSegment(sketch, "E377.MirrorCS", {"start": v(-83.3, 0) * mm, "end": v(-83.3, -10.23) * mm, "construction": true});
            skLineSegment(sketch, "E378.MirrorCS", {"start": v(-9.8, 0) * mm, "end": v(-9.8, -8.6) * mm, "construction": true});
            skLineSegment(sketch, "E379.MirrorCS", {"start": v(-82.9, -7.05) * mm, "end": v(-78.8, -7.05) * mm});
            skLineSegment(sketch, "E380.MirrorCS", {"start": v(-53.5, -7.05) * mm, "end": v(-49.4, -7.05) * mm});
            skLineSegment(sketch, "E381.MirrorCS", {"start": v(-24.9, -7.05) * mm, "end": v(-29, -7.05) * mm});
            skLineSegment(sketch, "E382.MirrorCS", {"start": v(-112.3, -7.05) * mm, "end": v(-108.2, -7.05) * mm});
            skLineSegment(sketch, "E383.MirrorCS", {"start": v(-54.3, -7.05) * mm, "end": v(-58.4, -7.05) * mm});
            skPoint(sketch, "E384.MirrorP", {"position": v(-56.35, -5) * mm});
            skLineSegment(sketch, "E385.MirrorCS", {"start": v(-147, 0) * mm, "end": v(-147, -8.6) * mm, "construction": true});
            skPoint(sketch, "E386.MirrorP", {"position": v(-144.55, -5) * mm});
            skLineSegment(sketch, "E387.MirrorCS", {"start": v(-122.5, 0) * mm, "end": v(-122.5, -10.23) * mm, "construction": true});
            skLineSegment(sketch, "E388.MirrorCS", {"start": v(-58.8, -5) * mm, "end": v(-160.81, -5) * mm});
            skLineSegment(sketch, "E389.MirrorCS", {"start": v(-19.6, 0) * mm, "end": v(-19.6, -8.6) * mm, "construction": true});
            skPoint(sketch, "E390.MirrorP", {"position": v(-110.25, -5) * mm});
            skPoint(sketch, "E391.MirrorP", {"position": v(-66.15, -5) * mm});
            skPoint(sketch, "E392.MirrorP", {"position": v(-26.95, -5) * mm});
            skPoint(sketch, "E393.MirrorP", {"position": v(-80.85, -5) * mm});
            skLineSegment(sketch, "E394.MirrorCS", {"start": v(-107.8, 0) * mm, "end": v(-107.8, -8.6) * mm, "construction": true});
            skLineSegment(sketch, "E395.MirrorCS", {"start": v(-103.3, -7.05) * mm, "end": v(-107.4, -7.05) * mm});
            skLineSegment(sketch, "E396.MirrorCS", {"start": v(-93.1, 0) * mm, "end": v(-93.1, -10.23) * mm, "construction": true});
            skLineSegment(sketch, "E397.MirrorCS", {"start": v(-44.5, -7.05) * mm, "end": v(-48.6, -7.05) * mm});
            skLineSegment(sketch, "E398.MirrorCS", {"start": v(-58.8, 0) * mm, "end": v(-58.8, -8.6) * mm, "construction": true});
            skLineSegment(sketch, "E399.MirrorCS", {"start": v(-15.1, -7.05) * mm, "end": v(-19.2, -7.05) * mm});
            skPoint(sketch, "E400.MirrorP", {"position": v(-105.35, -5) * mm});
            skPoint(sketch, "E401.MirrorP", {"position": v(-75.95, -5) * mm});
            skLineSegment(sketch, "E402.MirrorCS", {"start": v(-151.5, -7.05) * mm, "end": v(-147.4, -7.05) * mm});
            skLineSegment(sketch, "E403.MirrorCS", {"start": v(-29.4, 0) * mm, "end": v(-29.4, -8.6) * mm, "construction": true});
            skPoint(sketch, "E404.MirrorP", {"position": v(-41.65, -5) * mm});
            skPoint(sketch, "E405.MirrorP", {"position": v(-95.55, -5) * mm});
            skLineSegment(sketch, "E406.MirrorCS", {"start": v(-151.9, 0) * mm, "end": v(-151.9, -10.23) * mm, "construction": true});
            skLineSegment(sketch, "E407.MirrorCS", {"start": v(-88.2, 0) * mm, "end": v(-88.2, -8.6) * mm, "construction": true});
            skLineSegment(sketch, "E408.MirrorCS", {"start": v(-142.1, 0) * mm, "end": v(-142.1, -10.23) * mm, "construction": true});
            skLineSegment(sketch, "E409.MirrorCS", {"start": v(-73.9, -7.05) * mm, "end": v(-78, -7.05) * mm});
            skLineSegment(sketch, "E410.MirrorCS", {"start": v(-73.1, -7.05) * mm, "end": v(-69, -7.05) * mm});
            skLineSegment(sketch, "E411.MirrorCS", {"start": v(-83.7, -7.05) * mm, "end": v(-87.8, -7.05) * mm});
            skLineSegment(sketch, "E412.MirrorCS", {"start": v(-64.1, -7.05) * mm, "end": v(-68.2, -7.05) * mm});
            skLineSegment(sketch, "E413.MirrorCS", {"start": v(-122.1, -7.05) * mm, "end": v(-118, -7.05) * mm});
            skLineSegment(sketch, "E414.MirrorCS", {"start": v(-33.9, -7.05) * mm, "end": v(-29.8, -7.05) * mm});
            skLineSegment(sketch, "E415.MirrorCS", {"start": v(-63.3, -7.05) * mm, "end": v(-59.2, -7.05) * mm});
            skPoint(sketch, "E416.MirrorP", {"position": v(-36.75, -5) * mm});
            skPoint(sketch, "E417.MirrorP", {"position": v(-90.65, -5) * mm});
            skLineSegment(sketch, "E418.MirrorCS", {"start": v(-117.6, 0) * mm, "end": v(-117.6, -8.6) * mm, "construction": true});
            skPoint(sketch, "E419.MirrorP", {"position": v(-85.75, -5) * mm});
            skPoint(sketch, "E420.MirrorP", {"position": v(-134.75, -5) * mm});
            skLineSegment(sketch, "E421.MirrorCS", {"start": v(-112.7, 0) * mm, "end": v(-112.7, -10.23) * mm, "construction": true});
            skLineSegment(sketch, "E422.MirrorCS", {"start": v(-24.5, 0) * mm, "end": v(-24.5, -10.23) * mm, "construction": true});
            skLineSegment(sketch, "E423.MirrorCS", {"start": v(-137.2, 0) * mm, "end": v(-137.2, -8.6) * mm, "construction": true});
            skLineSegment(sketch, "E424.MirrorCS", {"start": v(-131.9, -7.05) * mm, "end": v(-127.8, -7.05) * mm});
            skLineSegment(sketch, "E425.MirrorCS", {"start": v(-98, -5) * mm, "end": v(4.01, -5) * mm});
            skLineSegment(sketch, "E426.MirrorCS", {"start": v(-132.3, 0) * mm, "end": v(-132.3, -10.23) * mm, "construction": true});
            skLineSegment(sketch, "E427.MirrorCS", {"start": v(-53.9, 0) * mm, "end": v(-53.9, -10.23) * mm, "construction": true});
            skPoint(sketch, "E428.MirrorP", {"position": v(-31.85, -5) * mm});
            skPoint(sketch, "E429.MirrorP", {"position": v(-61.25, -5) * mm});
            skLineSegment(sketch, "E430.bottom", {"start": v(-161.23, 8.6) * mm, "end": v(161.23, 8.6) * mm});
            skLineSegment(sketch, "E430.top", {"start": v(-161.23, -8.6) * mm, "end": v(161.23, -8.6) * mm});
            skLineSegment(sketch, "E430.left", {"start": v(-161.23, 8.6) * mm, "end": v(-161.23, -8.6) * mm});
            skLineSegment(sketch, "E430.right", {"start": v(161.23, 8.6) * mm, "end": v(161.23, -8.6) * mm});
            skPoint(sketch, "E430.middle", {"position": v(0, 0) * mm});
            skLineSegment(sketch, "E431", {"start": v(2.6, 8.6) * mm, "end": v(2.6, -8.6) * mm});
            skSolve(sketch);
        }
        {
            var Q0;
            {var subQ153=sQuery(id+"F0.wireOp",EDGE,"E3.top");Q0=makeQuery(id+"F0.imprint","IMPRINT",FACE,{"disambiguationData":[TD([[makeQuery(id+"F0.imprint","IMPRINT",EDGE,{"derivedFrom":subQ153}),-1.0]])]});}
            var Q1;
            {var subQ141=sQuery(id+"F0.wireOp",EDGE,"E3.bottom");Q1=makeQuery(id+"F0.imprint","IMPRINT",FACE,{"disambiguationData":[TD([[makeQuery(id+"F0.imprint","IMPRINT",EDGE,{"derivedFrom":subQ141}),1.0]])]});}
            extrude(context, id + "F1", {"entities" : qUnion([Q0, Q1]), "depth" : 15 * mm});
        }
    });
